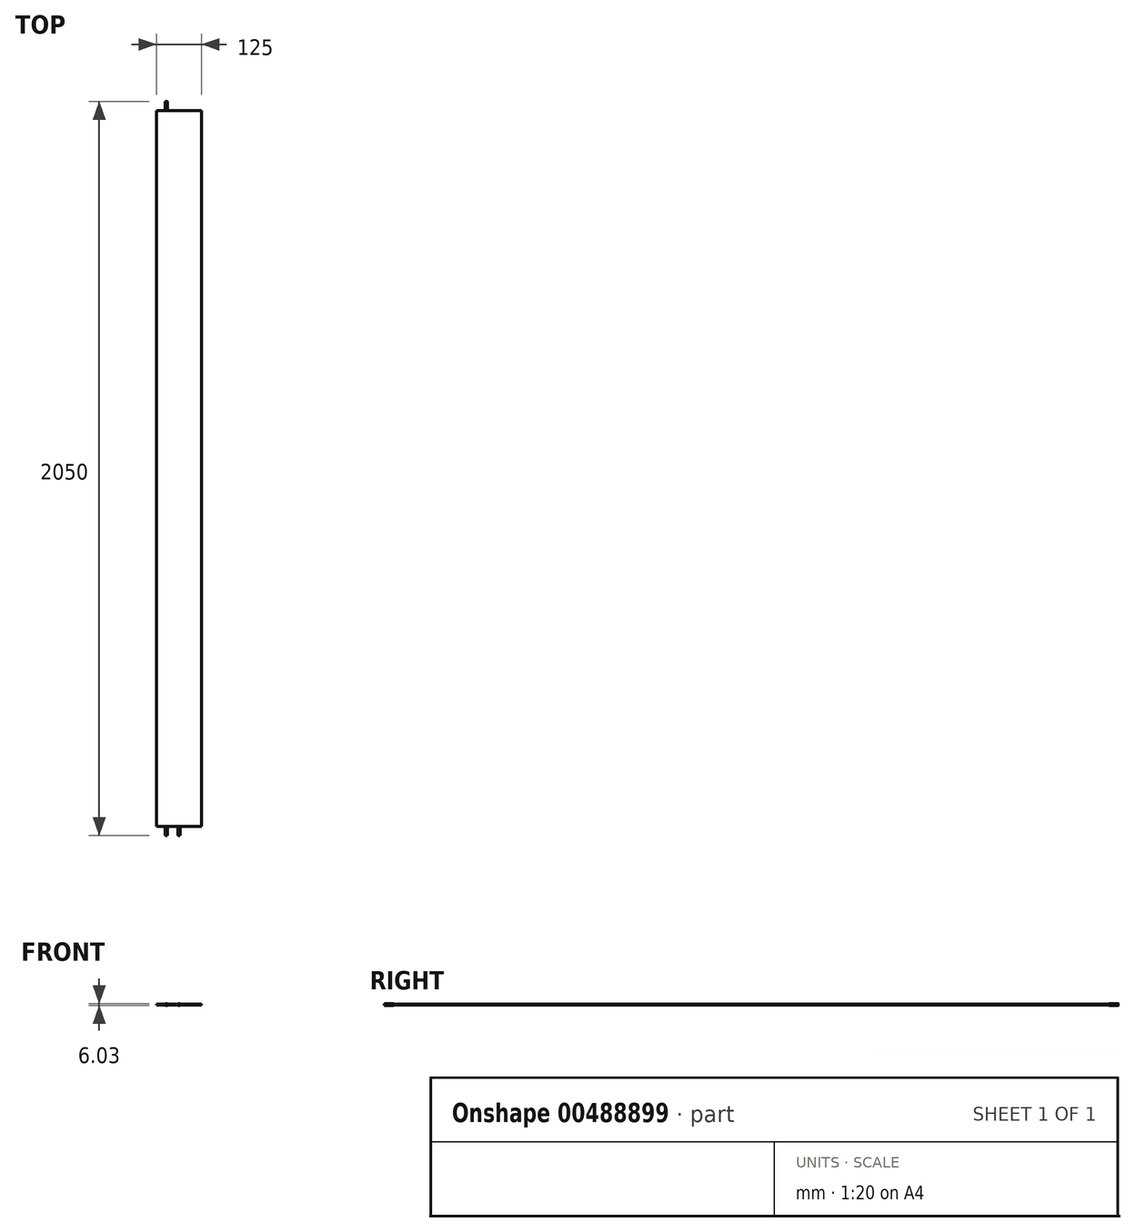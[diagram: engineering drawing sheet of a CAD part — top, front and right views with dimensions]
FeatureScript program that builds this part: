
annotation { "Feature Type Name" : "Feature", "Feature Type Description" : "" }
export const myFeature = defineFeature(function(context is Context, id is Id, definition is map)
    precondition{}
    {
        {
            var Q0;
            Q0=qCreatedBy(makeId("Top.planeOp"),FACE);
            var sketch = newSketch(context, id + "F0", { "sketchPlane" : qUnion([Q0])});
            skLineSegment(sketch, "E0.left", {"start": v(-30, 1855.8) * mm, "end": v(-30, -144.2) * mm});
            skLineSegment(sketch, "E0.right", {"start": v(95, 1855.8) * mm, "end": v(95, -144.2) * mm});
            skLineSegment(sketch, "E1", {"start": v(-30, 1855.8) * mm, "end": v(-5, 1855.8) * mm});
            skLineSegment(sketch, "E2", {"start": v(-5, 1855.8) * mm, "end": v(-5, 1875.8) * mm});
            skLineSegment(sketch, "E3", {"start": v(-5, 1875.8) * mm, "end": v(0, 1875.8) * mm});
            skLineSegment(sketch, "E4", {"start": v(0, 1875.8) * mm, "end": v(0, 1855.8) * mm});
            skLineSegment(sketch, "E5", {"start": v(0, 1855.8) * mm, "end": v(95, 1855.8) * mm});
            skLineSegment(sketch, "E6", {"start": v(-30, -144.2) * mm, "end": v(-5, -144.2) * mm});
            skLineSegment(sketch, "E7", {"start": v(-5, -144.2) * mm, "end": v(-5, -164.2) * mm});
            skLineSegment(sketch, "E8", {"start": v(35, -164.2) * mm, "end": v(35, -144.2) * mm});
            skLineSegment(sketch, "E9", {"start": v(35, -144.2) * mm, "end": v(95, -144.2) * mm});
            skLineSegment(sketch, "E10", {"start": v(-5, -164.2) * mm, "end": v(0, -164.2) * mm});
            skLineSegment(sketch, "E11", {"start": v(0, -164.2) * mm, "end": v(0, -144.2) * mm});
            skLineSegment(sketch, "E12", {"start": v(0, -144.2) * mm, "end": v(30, -144.2) * mm});
            skLineSegment(sketch, "E13", {"start": v(30, -144.2) * mm, "end": v(30, -164.2) * mm});
            skLineSegment(sketch, "E14", {"start": v(30, -164.2) * mm, "end": v(35, -164.2) * mm});
            skLineSegment(sketch, "E15", {"start": v(32.5, -120.58) * mm, "end": v(32.5, -185.54) * mm, "construction": true});
            skLineSegment(sketch, "E16", {"start": v(-30, -126.47) * mm, "end": v(95, -126.47) * mm, "construction": true});
            skPoint(sketch, "E17", {"position": v(32.5, -126.47) * mm});
            skPoint(sketch, "E18", {"position": v(32.5, -164.2) * mm});
            skSolve(sketch);
        }
        {
            var Q0;
            Q0=makeQuery(id+"F0.imprint","IMPRINT",FACE,{"disambiguationData":[TD([[makeQuery(id+"F0.imprint","IMPRINT",EDGE,{"derivedFrom":sQuery(id+"F0.wireOp",EDGE,"E0.bottom")}),-1.0]])]});
            var Q1;
            Q1=makeQuery(id+"F0.imprint","IMPRINT",FACE,{"disambiguationData":[TD([[makeQuery(id+"F0.imprint","IMPRINT",EDGE,{"derivedFrom":sQuery(id+"F0.wireOp",EDGE,"E0.left")}),1.0]])]});
            extrude(context, id + "F1", {"entities" : qUnion([Q0, Q1]), "depth" : 3 * mm});
        }
        {
            var Q0;
            Q0=makeQuery(id+"F1.opExtrude","SWEPT_FACE",FACE,{"disambiguationData":[OSD([sQuery(id+"F0.wireOp",EDGE,"E9")])]});
            var sketch = newSketch(context, id + "F2", { "sketchPlane" : qUnion([Q0])});
            skCircle(sketch, "E19", {"center": v(32.5, 1.5) * mm, "radius": 3 * mm});
            skSolve(sketch);
        }
        {
            var Q0;
            {var subQ1=sQuery(id+"F0.wireOp",EDGE,"E9");var subQ6=makeQuery(id+"F1.opExtrude","SWEPT_EDGE",EDGE,{"disambiguationData":[OSD([sQuery(id+"F0.wireOp",EDGE,"E8"),subQ1])]});Q0=makeQuery(id+"F2.imprint","IMPRINT",FACE,{"disambiguationData":[TD([[makeQuery(id+"F2.imprint","IMPRINT",EDGE,{"derivedFrom":subQ6}),-1.0]])]});}
            var Q1;
            {var subQ1=sQuery(id+"F0.wireOp",EDGE,"E9");var subQ6=makeQuery(id+"F1.opExtrude","SWEPT_EDGE",EDGE,{"disambiguationData":[OSD([sQuery(id+"F0.wireOp",EDGE,"E8"),subQ1])]});Q1=makeQuery(id+"F2.imprint","IMPRINT",FACE,{"disambiguationData":[TD([[makeQuery(id+"F2.imprint","IMPRINT",EDGE,{"derivedFrom":subQ6}),1.0]])]});}
            extrude(context, id + "F3", {"entities" : qUnion([Q0, Q1]), "operationType" : NewBodyOperationType.ADD, "depth" : 25 * mm});
        }
        {
            var Q0;
            Q0=makeQuery(id+"F1.opExtrude","SWEPT_FACE",FACE,{"disambiguationData":[OSD([sQuery(id+"F0.wireOp",EDGE,"E5")])]});
            var sketch = newSketch(context, id + "F4", { "sketchPlane" : qUnion([Q0])});
            skCircle(sketch, "E20", {"center": v(2.5, 1.5) * mm, "radius": 3 * mm});
            skSolve(sketch);
        }
        {
            var Q0;
            {var subQ1=sQuery(id+"F0.wireOp",EDGE,"E5");var subQ6=makeQuery(id+"F1.opExtrude","SWEPT_EDGE",EDGE,{"disambiguationData":[OSD([sQuery(id+"F0.wireOp",EDGE,"E4"),subQ1])]});Q0=makeQuery(id+"F4.imprint","IMPRINT",FACE,{"disambiguationData":[TD([[makeQuery(id+"F4.imprint","IMPRINT",EDGE,{"derivedFrom":subQ6}),1.0]])]});}
            var Q1;
            {var subQ1=sQuery(id+"F0.wireOp",EDGE,"E5");var subQ6=makeQuery(id+"F1.opExtrude","SWEPT_EDGE",EDGE,{"disambiguationData":[OSD([sQuery(id+"F0.wireOp",EDGE,"E4"),subQ1])]});Q1=makeQuery(id+"F4.imprint","IMPRINT",FACE,{"disambiguationData":[TD([[makeQuery(id+"F4.imprint","IMPRINT",EDGE,{"derivedFrom":subQ6}),-1.0]])]});}
            extrude(context, id + "F5", {"entities" : qUnion([Q0, Q1]), "operationType" : NewBodyOperationType.ADD, "depth" : 25 * mm});
        }
        {
            var Q0;
            Q0=makeQuery(id+"F1.opExtrude","SWEPT_FACE",FACE,{"disambiguationData":[OSD([sQuery(id+"F0.wireOp",EDGE,"E12")])]});
            var sketch = newSketch(context, id + "F6", { "sketchPlane" : qUnion([Q0])});
            skCircle(sketch, "E21", {"center": v(-2.5, 1.53) * mm, "radius": 3 * mm});
            skSolve(sketch);
        }
        {
            var Q0;
            {var subQ1=sQuery(id+"F0.wireOp",EDGE,"E12");var subQ6=makeQuery(id+"F1.opExtrude","SWEPT_EDGE",EDGE,{"disambiguationData":[OSD([sQuery(id+"F0.wireOp",EDGE,"E11"),subQ1])]});Q0=makeQuery(id+"F6.imprint","IMPRINT",FACE,{"disambiguationData":[TD([[makeQuery(id+"F6.imprint","IMPRINT",EDGE,{"derivedFrom":subQ6}),1.0]])]});}
            var Q1;
            {var subQ1=sQuery(id+"F0.wireOp",EDGE,"E12");var subQ6=makeQuery(id+"F1.opExtrude","SWEPT_EDGE",EDGE,{"disambiguationData":[OSD([sQuery(id+"F0.wireOp",EDGE,"E11"),subQ1])]});Q1=makeQuery(id+"F6.imprint","IMPRINT",FACE,{"disambiguationData":[TD([[makeQuery(id+"F6.imprint","IMPRINT",EDGE,{"derivedFrom":subQ6}),-1.0]])]});}
            extrude(context, id + "F7", {"entities" : qUnion([Q0, Q1]), "operationType" : NewBodyOperationType.ADD, "depth" : 25 * mm, "offsetDistance" : 25 * mm});
        }
    });
